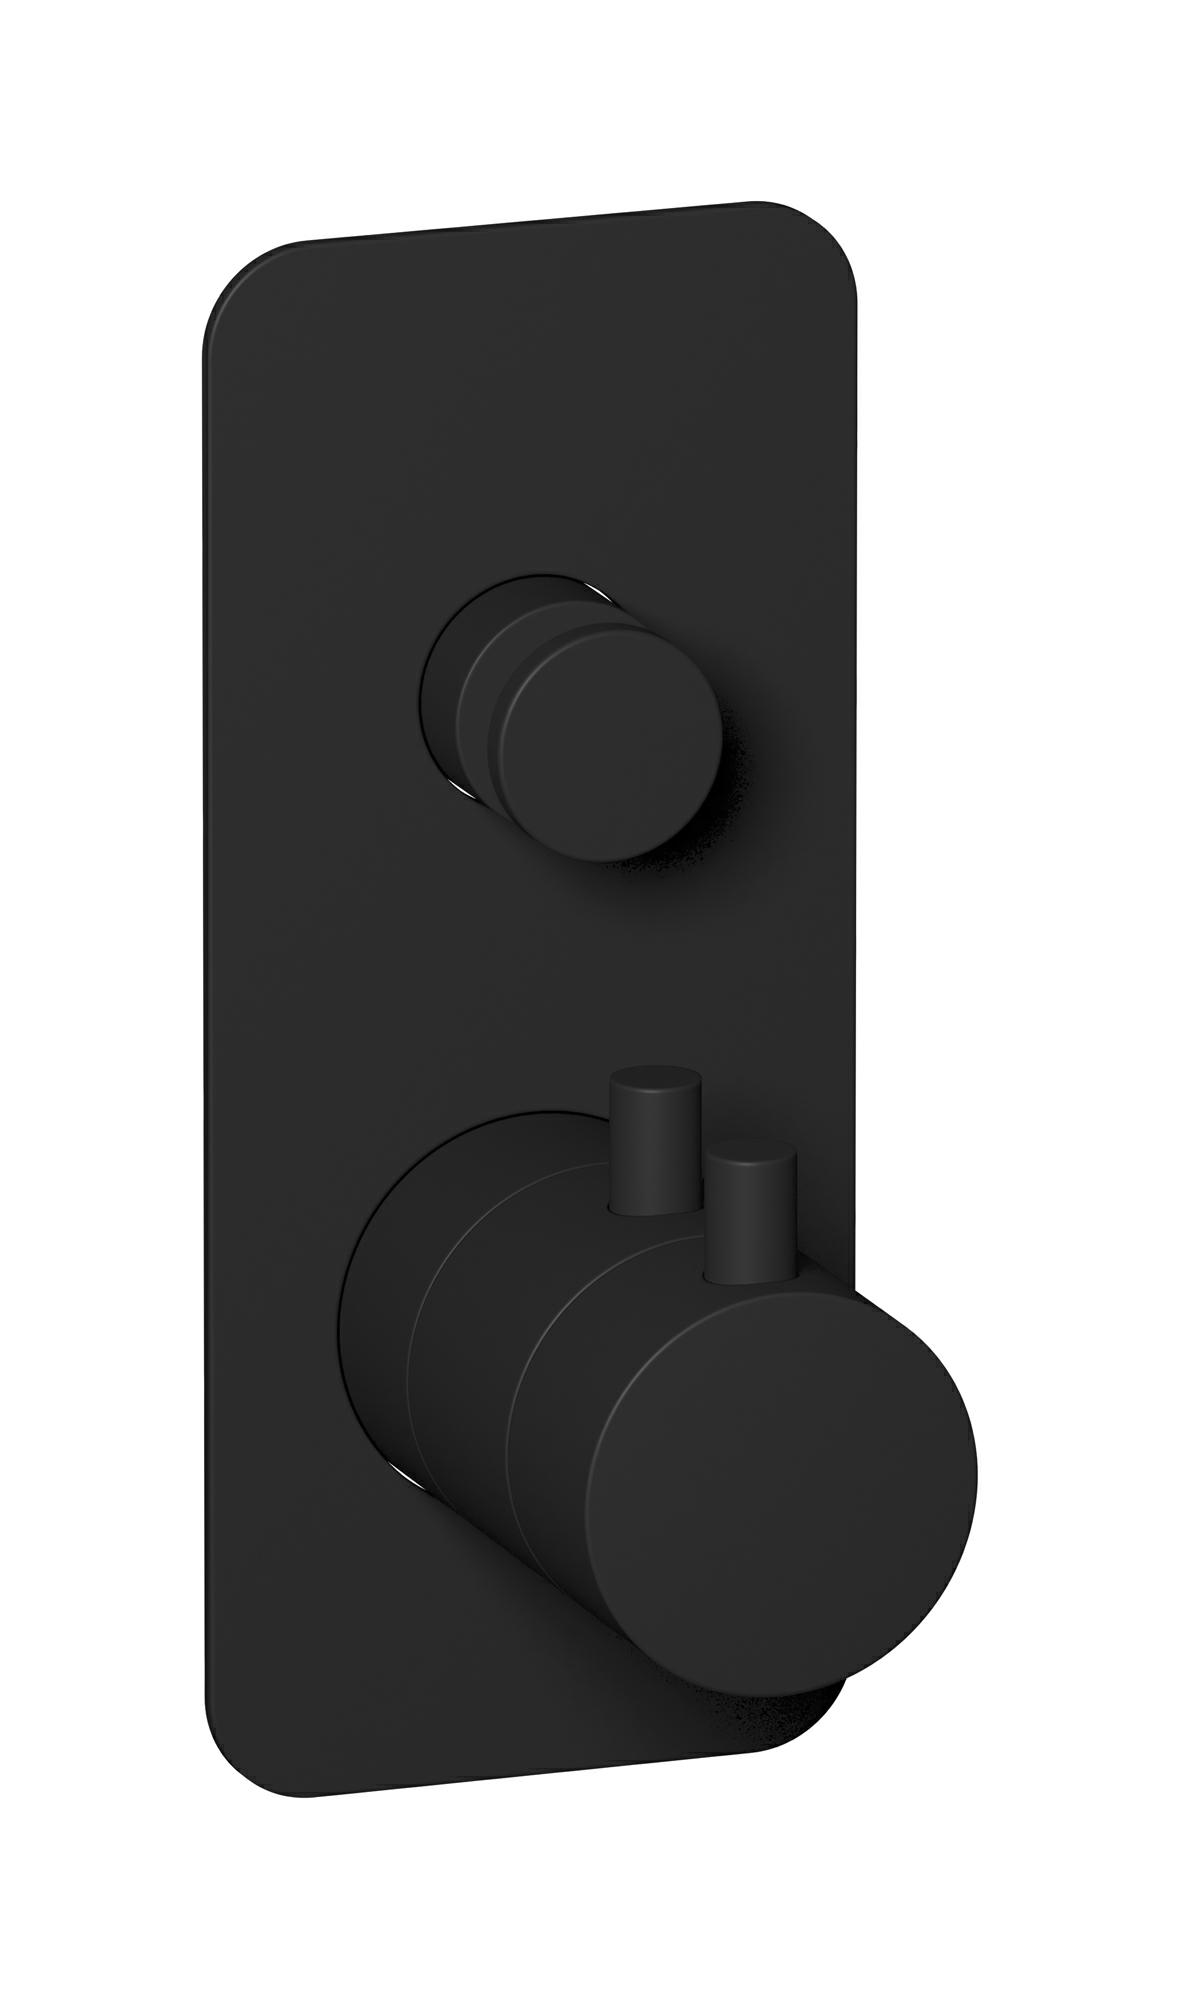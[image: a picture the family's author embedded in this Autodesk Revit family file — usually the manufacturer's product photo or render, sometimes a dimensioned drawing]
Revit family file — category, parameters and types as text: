
# Revit family: MT610
name_source: partatom
category: Apparecchi idraulici
units: mm (PartAtom-declared; Revit-internal decimal feet)

## family parameters
Basato su piano di lavoro = No
Condiviso = No
Mantieni orientamento annotazione = No
Numero OmniClass = 23.45.55.17
Punto di calcolo locali = No
Quota connettore circolare = Usa diametro
Sempre verticale = Sì
Taglio con vuoti quando caricato = No
Tipo di parte = Normale
Titolo OmniClass = Mixing Faucets

## types (13) — shared parameters
Cold water inlet = 10 mm  [stored 0.0328084 ft]
Commenti sul tipo = Two ways wall shower thermostatic valve
Connessione CW = No
Connessione HW = No
Connessione di scarico = No
Connessione di ventilazione = No
Descrizione = Two ways wall shower thermostatic valve
Hot water inlet = 10 mm  [stored 0.0328084 ft]
Produttore = IB Rubinetterie S.p.A.
URL = https://www.weareib.it
zero-valued in all types: Prospetto di default

## per-type parameters (varying)
| type | Finishes surface | Immagine tipo | Modello |
| Chrome | IB_Chrome | MT610CC.jpg | MT610CC |
| Brushed nickel | IB_Brushed nickel | MT610SS.jpg | MT610SS |
| Matt black | IB_matt black | MT610NP.jpg | MT610NP |
| Matt white | IB_matt white | MT610BO.jpg | MT610BO |
| Natural brass | IB_Brass | MT610ON.jpg | MT610ON |
| Black chrome | IB_Black chrome | MT610CF.jpg | MT610CF |
| Brushed black chrome | IB_Brushed black chrome | MT610CS.jpg | MT610CS |
| Pale gold | IB_Pale gold | MT610II.jpg | MT610II |
| Brushed pale gold | IB_brushed pale gold | MT610IS.jpg | MT610IS |
| Rose gold | IB_Rose gold | MT610RS.jpg | MT610RS |
| Brushed rose gold | IB_Brushed rose gold | MT610SR.jpg | MT610SR |
| Gold | IB_gold | MT610OO.jpg | MT610OO |
| Brushed gold | IB_brushed gold | MT610OS.jpg | MT610OS |

note: [stored X ft] marks values corroborated as IEEE doubles in the binary element streams (Revit-internal decimal feet)
